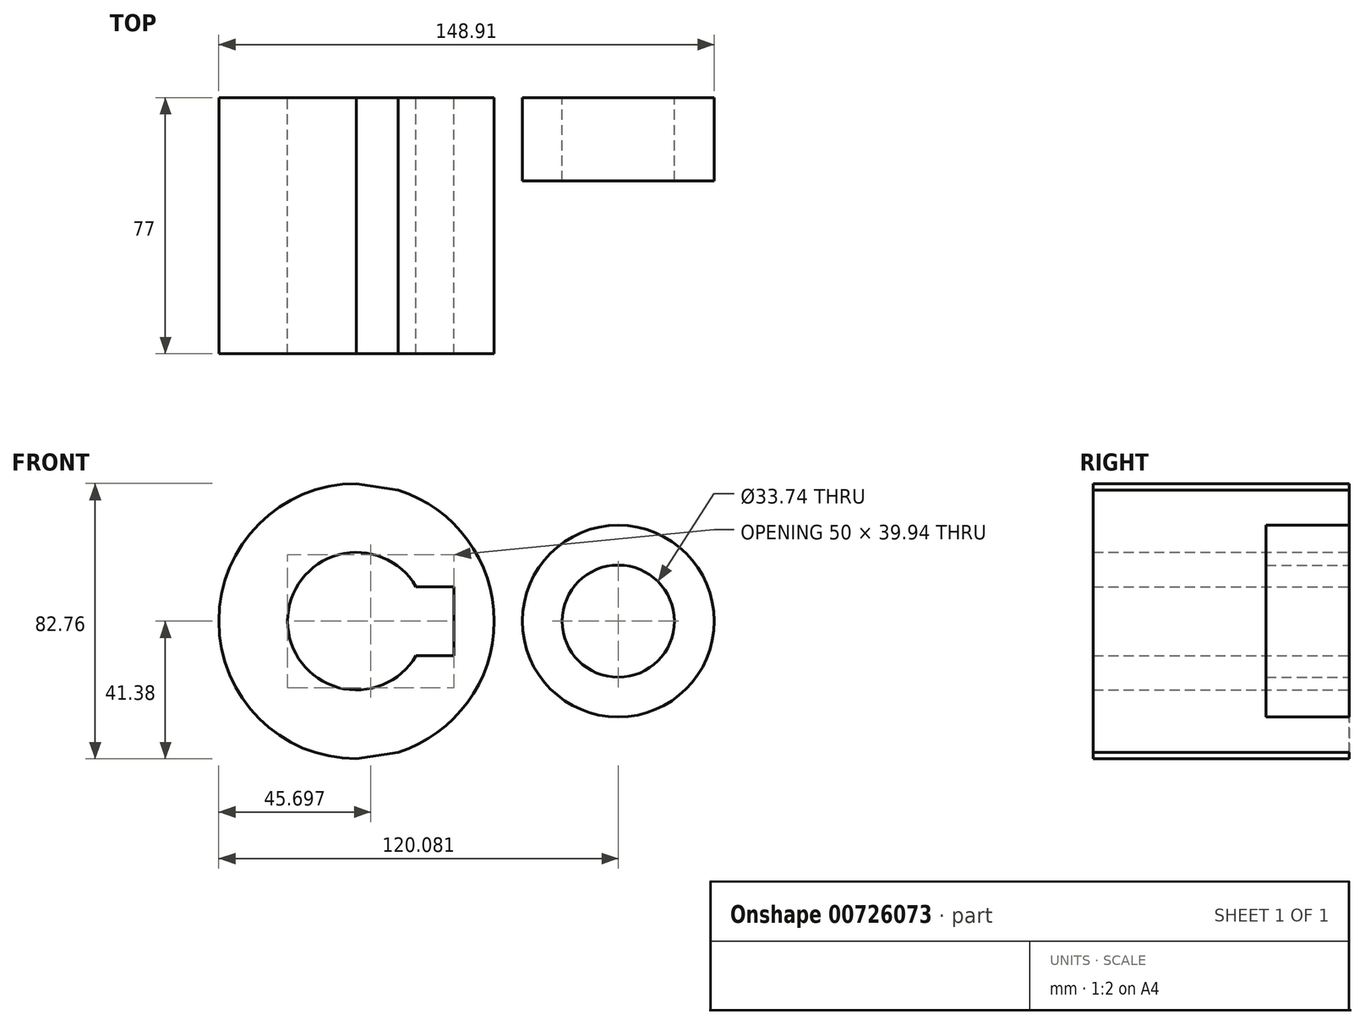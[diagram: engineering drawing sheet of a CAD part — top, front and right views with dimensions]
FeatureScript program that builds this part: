
annotation { "Feature Type Name" : "Feature", "Feature Type Description" : "" }
export const myFeature = defineFeature(function(context is Context, id is Id, definition is map)
    precondition{}
    {
        {
            var Q0;
            Q0=qCreatedBy(makeId("Front.planeOp"),FACE);
            var sketch = newSketch(context, id + "F0", { "sketchPlane" : qUnion([Q0])});
            skCircle(sketch, "E0", {"center": v(0, 0) * mm, "radius": 41.38 * mm});
            skCircle(sketch, "E1", {"center": v(78.7, 0) * mm, "radius": 28.83 * mm});
            skLineSegment(sketch, "E2", {"start": v(0, 41.38) * mm, "end": v(83.12, 28.5) * mm});
            skLineSegment(sketch, "E3", {"start": v(0, -41.38) * mm, "end": v(83.12, -28.5) * mm});
            skCircle(sketch, "E4", {"center": v(0, 0) * mm, "radius": 20.68 * mm});
            skCircle(sketch, "E5", {"center": v(78.7, 0) * mm, "radius": 16.87 * mm});
            skLineSegment(sketch, "E6.bottom", {"start": v(29.32, -10.38) * mm, "end": v(-29.32, -10.38) * mm});
            skLineSegment(sketch, "E6.top", {"start": v(29.32, 10.38) * mm, "end": v(-29.32, 10.38) * mm});
            skLineSegment(sketch, "E6.left", {"start": v(29.32, -10.38) * mm, "end": v(29.32, 10.38) * mm});
            skLineSegment(sketch, "E6.right", {"start": v(-29.32, -10.38) * mm, "end": v(-29.32, 10.38) * mm});
            skSolve(sketch);
        }
        {
            var Q0;
            {var subQ4=sQuery(id+"F0.wireOp",EDGE,"E6.left");Q0=makeQuery(id+"F0.imprint","IMPRINT",FACE,{"disambiguationData":[TD([[makeQuery(id+"F0.imprint","IMPRINT",EDGE,{"derivedFrom":subQ4}),-1.0]])]});}
            extrude(context, id + "F1", {"entities" : qUnion([Q0]), "depth" : 25.4 * mm, "offsetDistance" : 25 * mm});
        }
        {
            var Q0;
            {var subQ5=sQuery(id+"F0.wireOp",EDGE,"E6.right");Q0=makeQuery(id+"F0.imprint","IMPRINT",FACE,{"disambiguationData":[TD([[makeQuery(id+"F0.imprint","IMPRINT",EDGE,{"derivedFrom":subQ5}),-1.0]])]});}
            extrude(context, id + "F2", {"entities" : qUnion([Q0]), "operationType" : NewBodyOperationType.ADD, "depth" : 77 * mm, "offsetDistance" : 25 * mm});
        }
        {
            var Q0;
            {var subQ0=sQuery(id+"F0.wireOp",EDGE,"E2");var subQ1=sQuery(id+"F0.wireOp",EDGE,"E0");var subQ2=makeQuery(id+"F0.imprint","INTERSECT",VERTEX,{"disambiguationData":[OD(1.0)],"derivedFrom":[subQ1,subQ0]});Q0=makeQuery(id+"F0.imprint","IMPRINT",FACE,{"disambiguationData":[TD([[makeQuery(id+"F0.imprint","IMPRINT",EDGE,{"disambiguationData":[TD([[subQ2,1.0]])],"derivedFrom":subQ1}),-1.0]])]});}
            var Q1;
            Q1=makeQuery(id+"F0.imprint","IMPRINT",FACE,{"disambiguationData":[TD([[makeQuery(id+"F0.imprint","IMPRINT",EDGE,{"derivedFrom":sQuery(id+"F0.wireOp",EDGE,"E5")}),-1.0]])]});
            extrude(context, id + "F3", {"entities" : qUnion([Q0, Q1]), "operationType" : NewBodyOperationType.ADD, "depth" : 25 * mm, "offsetDistance" : 25 * mm});
        }
        {
            var Q0;
            {var subQ0=sQuery(id+"F0.wireOp",EDGE,"E2");var subQ1=sQuery(id+"F0.wireOp",EDGE,"E0");var subQ2=makeQuery(id+"F0.imprint","INTERSECT",VERTEX,{"disambiguationData":[OD(0.0)],"derivedFrom":[subQ1,subQ0]});Q0=makeQuery(id+"F0.imprint","IMPRINT",FACE,{"disambiguationData":[TD([[makeQuery(id+"F0.imprint","IMPRINT",EDGE,{"disambiguationData":[TD([[subQ2,1.0]])],"derivedFrom":subQ1}),1.0]])]});}
            var Q1;
            {var subQ4=sQuery(id+"F0.wireOp",EDGE,"E6.left");Q1=makeQuery(id+"F0.imprint","IMPRINT",FACE,{"disambiguationData":[TD([[makeQuery(id+"F0.imprint","IMPRINT",EDGE,{"derivedFrom":subQ4}),-1.0]])]});}
            extrude(context, id + "F4", {"entities" : qUnion([Q0, Q1]), "operationType" : NewBodyOperationType.ADD, "depth" : 77 * mm, "offsetDistance" : 25 * mm});
        }
    });
